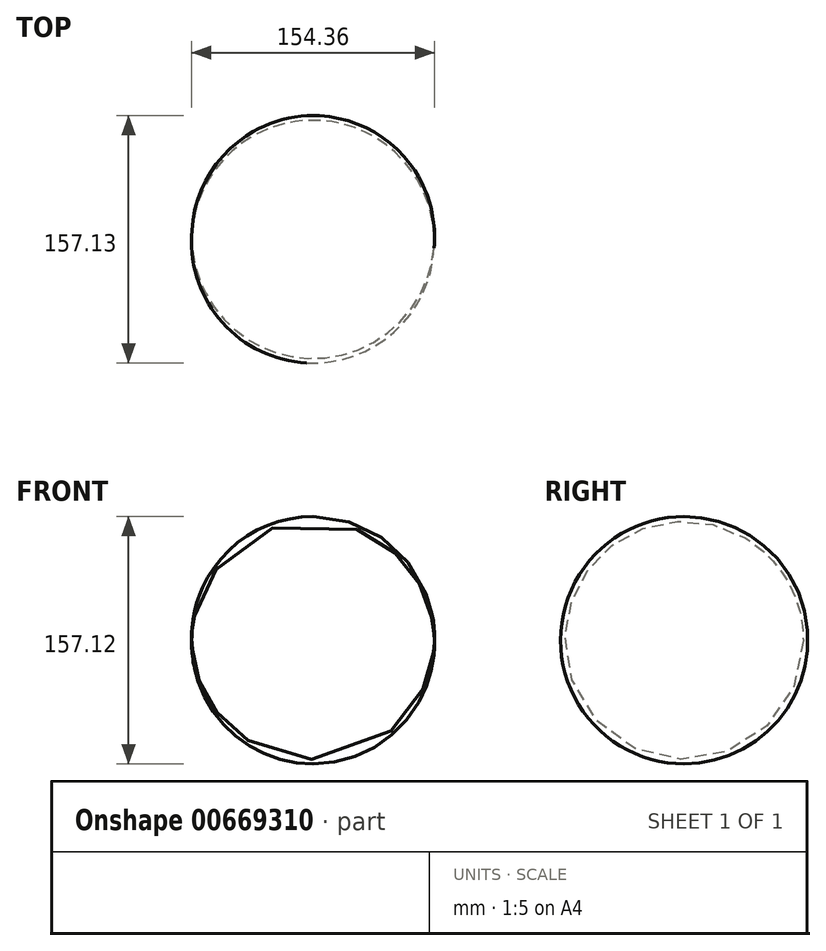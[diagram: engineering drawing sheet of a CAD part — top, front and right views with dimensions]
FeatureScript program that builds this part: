
annotation { "Feature Type Name" : "Feature", "Feature Type Description" : "" }
export const myFeature = defineFeature(function(context is Context, id is Id, definition is map)
    precondition{}
    {
        {
            var Q0;
            Q0=qCreatedBy(makeId("Top.planeOp"),FACE);
            var sketch = newSketch(context, id + "F0", { "sketchPlane" : qUnion([Q0])});
            skLineSegment(sketch, "E0", {"start": v(-76.35, -6.2) * mm, "end": v(77.6, -14.52) * mm});
            skArc(sketch, "E1", {"start": v(77.6, -14.52) * mm, "mid": v(4.86, 68.08) * mm, "end": v(-76.35, -6.2) * mm});
            skSolve(sketch);
        }
        {
            var Q0;
            Q0=makeQuery(id+"F0.imprint","IMPRINT",FACE,{"disambiguationData":[TD([[makeQuery(id+"F0.imprint","IMPRINT",EDGE,{"derivedFrom":sQuery(id+"F0.wireOp",EDGE,"E0")}),1.0]])]});
            var Q1;
            Q1=sQuery(id+"F0.wireOp",EDGE,"E0");
            revolve(context, id + "F1", {"entities" : qUnion([Q0]), "axis" : qUnion([Q1]), "revolveType" : RevolveType.FULL});
        }
    });
